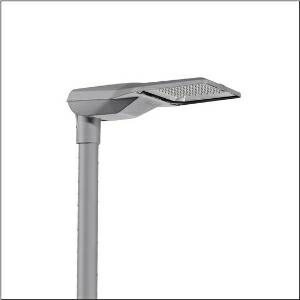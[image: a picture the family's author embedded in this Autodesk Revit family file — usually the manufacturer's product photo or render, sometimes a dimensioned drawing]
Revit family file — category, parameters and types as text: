
# Revit family: streetlight_sl_21_iq_midi___st1_0a_5xe3d41g08nb_8322
name_source: partatom
category: Lighting Fixtures
units: mm (PartAtom-declared; Revit-internal decimal feet)

## family parameters
Cut with Voids When Loaded = No
Host = Face
Light Source = No
Part Type = Normal
Room Calculation Point = No
Round Connector Dimension = Use Diameter
Shared = No

## types (1)
- --- (1 x LED, 24250 lm, 155.5 W, 4000K)
    Apparent Load = 155 VA
    CIE Flux Codes = 40 73 97 100 100
    Color Rendering = 70
    Color Temperature = 4000K
    Default Elevation = 1800 mm
    Description = Streetlight SL 21 iQ midi, mast luminaire, primary light control with lens, of PMMA, primary optical cover: cover, of toughened safety glass, transparent, light distribution: ST1.0a, light emission: direct distribution, primary light characteristic: asymmetric, installation type: post-top, side-entry, LED, High Power LED, rated luminous flux: 24.250lm, luminous efficacy: 156lm/W, light colour: 740, colour temperature: 4000K, control gear: iQ Street-Remote, control: Street-Remote, Auto-Match, Temp-Guard, Lumen-Switch, Night-Set, Smart-Wire, Light-Fading, Desk-Remote (wireless, voltage-free reading and setting of iQ features in the workshop via application-optimized NFC function/RFID function), optimised constant luminous flux control (CLO 2.0), pre-setting: linear dimming characteristic, mains connection: 230..240V, AC, 50/60Hz, start of lifetime: 156W, end of service life: 162W, reduction: 69W, luminaire housing, of diecast aluminium, powder-coated, Siteco® metallic grey (DB 702S), corrosivity category C5 mid according to DIN EN ISO 12944, please order mast flange separately, inclination adjustable: 0°, 5°, 10°, 15°, sealing non-destructively replaceable, multi-level sealing system, length: 644mm, width: 335mm, height: 110mm, mast flange for spigot size: 42mm (side-entry): 5XC10008XM4, 60/48mm (side-entry/post-top): 5XC10108XM2, 76/60mm (side-entry/post-top): 5XC10108XM1, mounting height: 4..8m, protection rating (complete): IP66, insulation class (complete): insulation class II (safety insulation), certification: CE, ENEC, ENEC+, VDE, impact resistance: IK10, permissible operating ambient temperature for outdoor applications: -40..+50°C, standard-compliant lighting for roads and squares, packaging unit: 1 piece

Light Distribution: ST1.0a
    Height = 111 mm
    Lamp = 1 x LED
    Lamp Light Flux = 24250 lm
    Lamp Power = 155.5 W
    Lamp count = 1
    Length = 644 mm
    Luminous efficacy = 156 lm/W
    Manufacturer = Siteco
    ModVariant = No
    Model = 5XE3D41G08NB
    Number of Poles = 1
    OnlyDefault = Yes
    Power Factor = 1
    Product Name = Streetlight SL 21 iQ midi | ST1.0a
    Product group = mast luminaire | pylon top
    ProductGroupID = 6100
    Protection Class = Protection class II
    Protection Degree = IP 66
    RLX_Detail_Level = 1
    RLX_Emergency_Light_Flux = 0 lm
    RLX_Emergency_Type = 0
    RLX_Emergency_Type_DB = No
    RlxData = <blob elided: 27205 chars, md5=bfa8f276>
    Socket = socket
    Standby Power = 0 W
    System Light Flux = 24250 lm
    System Power = 155 W
    Type Comments = factory setting: luminous flux: 100 % | dim-lin: 254 | 823 mA
    Type Image = l_1004298.jpg
    URL = http://relux.com
    VarID = @adj_192235
    Voltage = 0 V
    Weight = 0.00 kg
    Width = 336 mm

## geometry (parser evidence)
native form markers: Blend x4, Sweep x10
no freeform markers — native parametric forms only
